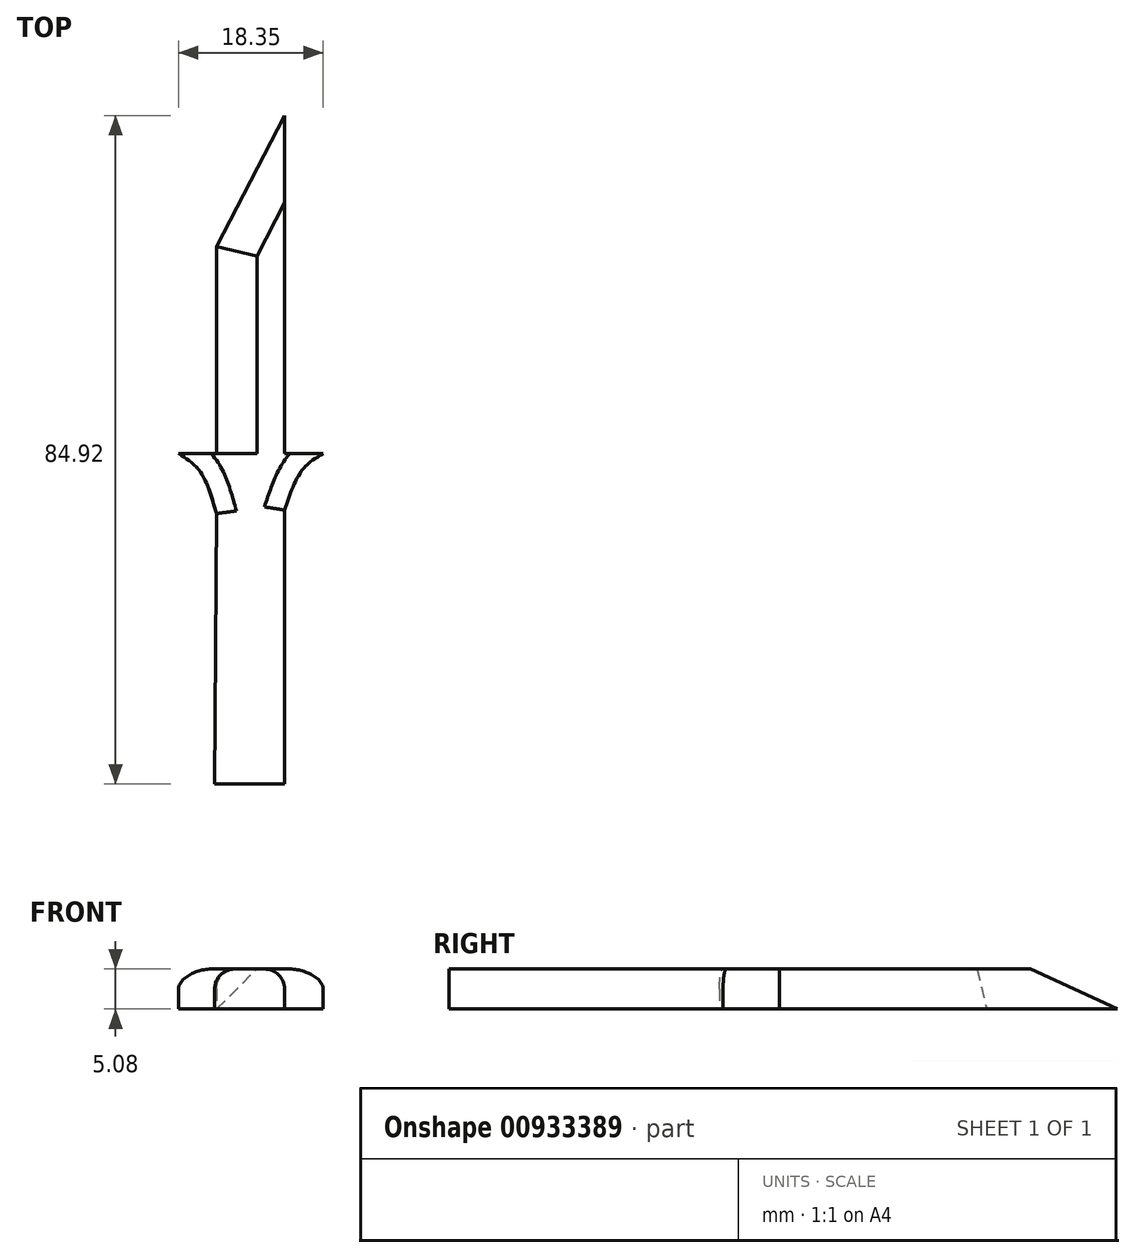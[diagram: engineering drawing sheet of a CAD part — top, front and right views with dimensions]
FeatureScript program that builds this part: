
annotation { "Feature Type Name" : "Feature", "Feature Type Description" : "" }
export const myFeature = defineFeature(function(context is Context, id is Id, definition is map)
    precondition{}
    {
        {
            var Q0;
            Q0=qCreatedBy(makeId("Top.planeOp"),FACE);
            var sketch = newSketch(context, id + "F0", { "sketchPlane" : qUnion([Q0])});
            skLineSegment(sketch, "E0", {"start": v(-59.16, 21.47) * mm, "end": v(-59.16, 47.8) * mm});
            skLineSegment(sketch, "E1", {"start": v(-59.16, 47.8) * mm, "end": v(-50.57, 64.42) * mm});
            skLineSegment(sketch, "E2", {"start": v(-50.57, 64.42) * mm, "end": v(-50.57, -20.5) * mm});
            skLineSegment(sketch, "E3", {"start": v(-50.57, -20.5) * mm, "end": v(-59.44, -20.5) * mm});
            skLineSegment(sketch, "E4", {"start": v(-59.44, -20.5) * mm, "end": v(-59.16, 21.47) * mm});
            skLineSegment(sketch, "E5", {"start": v(-59.16, 21.47) * mm, "end": v(-64, 21.47) * mm});
            skFitSpline(sketch, "E6", {"points": [v(-64, 21.47) * mm, v(-61.29, 19.2) * mm, v(-59.2, 13.86) * mm], "startDerivative": vector(6.73, -4.2) * mm, "endDerivative": vector(3.02, -10.77) * mm});
            skLineSegment(sketch, "E7", {"start": v(-59.16, 21.47) * mm, "end": v(-50.57, 21.47) * mm});
            skPoint(sketch, "E7.endSnap0", {"position": v(-50.57, 21.96) * mm});
            skLineSegment(sketch, "E8", {"start": v(-50.57, 21.47) * mm, "end": v(-45.66, 21.47) * mm});
            skFitSpline(sketch, "E9", {"points": [v(-45.66, 21.47) * mm, v(-48.3, 19.4) * mm, v(-50.57, 14.3) * mm], "startDerivative": vector(-6.5, -3.82) * mm, "endDerivative": vector(-3.45, -10.26) * mm});
            skSolve(sketch);
        }
        {
            var Q0;
            Q0 = qSketchRegion(id + "F0", true);
            extrude(context, id + "F1", {"entities" : qUnion([Q0]), "depth" : 5.08 * mm, "offsetDistance" : 25.4 * mm});
        }
        {
            var Q0;
            Q0=makeQuery(id+"F1.opExtrude","CAP_EDGE",EDGE,{"disambiguationData":[OSD([sQuery(id+"F0.wireOp",EDGE,"E0")])],"isStart":false});
            var Q1;
            Q1=makeQuery(id+"F1.opExtrude","CAP_EDGE",EDGE,{"disambiguationData":[OSD([sQuery(id+"F0.wireOp",EDGE,"E1")])],"isStart":false});
            chamfer(context, id + "F2", {"entities" : qUnion([Q0, Q1]), "width" : 5.08 * mm, "tangentPropagation" : true});
        }
        {
            var Q0;
            Q0=makeQuery(id+"F1.opExtrude","CAP_EDGE",EDGE,{"disambiguationData":[OSD([sQuery(id+"F0.wireOp",EDGE,"E4")])],"isStart":false});
            var Q1;
            {var subQ0=sQuery(id+"F0.wireOp",EDGE,"E2");Q1=makeQuery(id+"F1.opExtrude","CAP_EDGE",EDGE,{"disambiguationData":[OSD([subQ0]),TDD([makeQuery(id+"F0.imprint","IMPRINT",EDGE,{"disambiguationData":[TD([[makeQuery(id+"F0.imprint","INTERSECT",VERTEX,{"derivedFrom":[subQ0,sQuery(id+"F0.wireOp",EDGE,"E3")]}),1.0]])],"derivedFrom":subQ0})])],"isStart":false});}
            var Q2;
            Q2=makeQuery(id+"F1.opExtrude","CAP_EDGE",EDGE,{"disambiguationData":[OSD([sQuery(id+"F0.wireOp",EDGE,"E6")])],"isStart":false});
            var Q3;
            Q3=makeQuery(id+"F1.opExtrude","CAP_EDGE",EDGE,{"disambiguationData":[OSD([sQuery(id+"F0.wireOp",EDGE,"E9")])],"isStart":false});
            fillet(context, id + "F3", {"entities" : qUnion([Q0, Q1, Q2, Q3]), "radius" : 2.54 * mm, "tangentPropagation" : true, "allowEdgeOverflow" : false});
        }
    });
